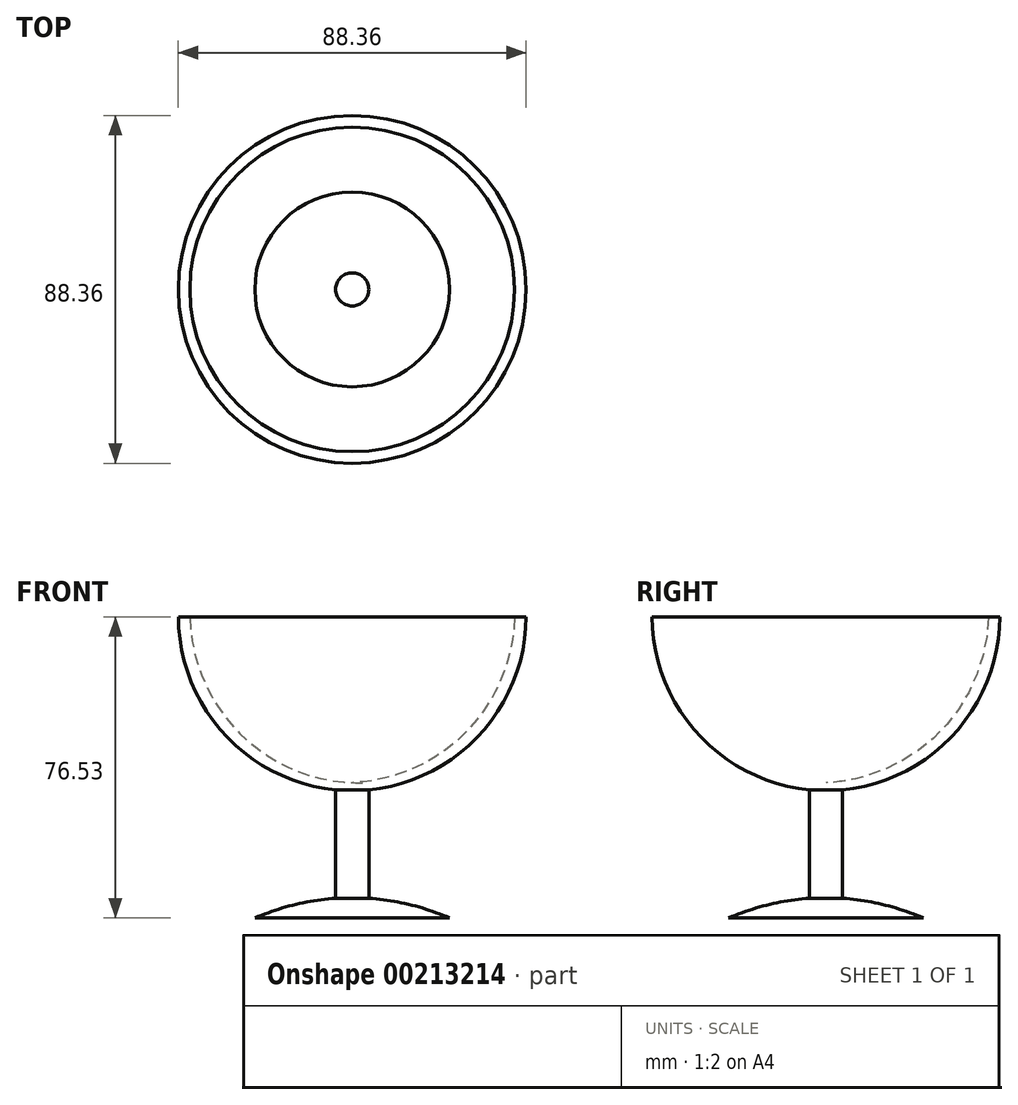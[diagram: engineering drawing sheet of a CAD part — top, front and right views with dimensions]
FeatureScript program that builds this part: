
annotation { "Feature Type Name" : "Feature", "Feature Type Description" : "" }
export const myFeature = defineFeature(function(context is Context, id is Id, definition is map)
    precondition{}
    {
        {
            var Q0;
            Q0=qCreatedBy(makeId("Front.planeOp"),FACE);
            var sketch = newSketch(context, id + "F0", { "sketchPlane" : qUnion([Q0])});
            skArc(sketch, "E0", {"start": v(-44.18, 76.53) * mm, "mid": v(-32.65, 46.87) * mm, "end": v(-4.22, 32.57) * mm});
            skLineSegment(sketch, "E1", {"start": v(-4.22, 32.57) * mm, "end": v(-4.22, 5.04) * mm});
            skArc(sketch, "E2", {"start": v(-41.24, 76.34) * mm, "mid": v(-28.88, 47.24) * mm, "end": v(0, 34.37) * mm});
            skArc(sketch, "E3", {"start": v(-4.22, 5.04) * mm, "mid": v(-14.69, 3.36) * mm, "end": v(-24.75, 0) * mm});
            skPoint(sketch, "E4.orphan", {"position": v(0, 32.35) * mm});
            skLineSegment(sketch, "E5", {"start": v(-41.24, 76.34) * mm, "end": v(-44.18, 76.53) * mm});
            skLineSegment(sketch, "E6", {"start": v(0, 34.37) * mm, "end": v(0, 0) * mm});
            skLineSegment(sketch, "E7", {"start": v(0, 0) * mm, "end": v(-24.75, 0) * mm});
            skSolve(sketch);
        }
        {
            var Q0;
            Q0=makeQuery(id+"F0.imprint","IMPRINT",FACE,{"disambiguationData":[TD([[makeQuery(id+"F0.imprint","IMPRINT",EDGE,{"derivedFrom":sQuery(id+"F0.wireOp",EDGE,"E0")}),1.0]])]});
            var Q1;
            Q1=sQuery(id+"F0.wireOp",EDGE,"E6");
            revolve(context, id + "F1", {"entities" : qUnion([Q0]), "axis" : qUnion([Q1]), "revolveType" : RevolveType.FULL});
        }
    });
